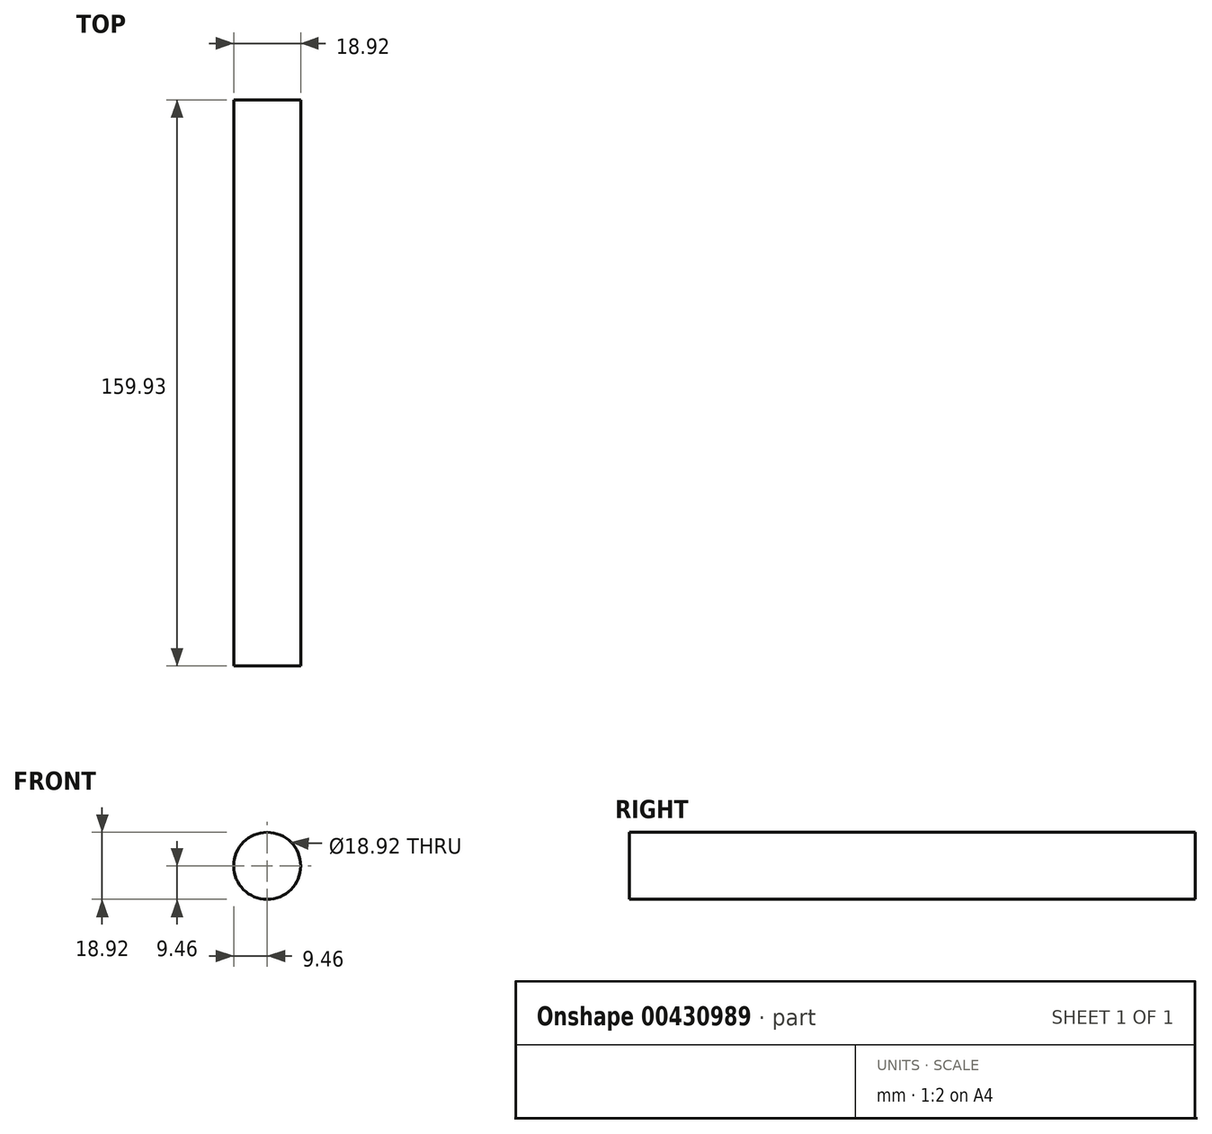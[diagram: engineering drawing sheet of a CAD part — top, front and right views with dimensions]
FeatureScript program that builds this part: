
annotation { "Feature Type Name" : "Feature", "Feature Type Description" : "" }
export const myFeature = defineFeature(function(context is Context, id is Id, definition is map)
    precondition{}
    {
        {
            var Q0;
            Q0=qCreatedBy(makeId("Front.planeOp"),FACE);
            var sketch = newSketch(context, id + "F0", { "sketchPlane" : qUnion([Q0])});
            skCircle(sketch, "E0", {"center": v(0, 0) * mm, "radius": 1.33 * mm});
            skCircle(sketch, "E1", {"center": v(0, 0) * mm, "radius": 3.12 * mm});
            skCircle(sketch, "E2", {"center": v(0, 0) * mm, "radius": 9.46 * mm});
            skSolve(sketch);
        }
        {
            var Q0;
            Q0=sQuery(id+"F0.wireOp",EDGE,"E2");
            extrude(context, id + "F1", {"bodyType" : ToolBodyType.SURFACE, "surfaceEntities" : qUnion([Q0]), "oppositeDirection" : true, "depth" : 159.93 * mm});
        }
    });
